# Revit family: Furniture-Lighted_Medicine_Cabinet-KOHLER-Family_Care-K-25237T_1
name_source: partatom
category: Lighting Fixtures
units: mm (PartAtom-declared; Revit-internal decimal feet)

## family parameters
Cut with Voids When Loaded = No
Host = Face
Light Source = Yes
Maintain Annotation Orientation = No
OmniClass Number = 23.25.53.11.13.11
OmniClass Title = Medicine Cabinet
Part Type = Normal
Room Calculation Point = No
Round Connector Dimension = Use Diameter
Shared = No

## types (2) — shared parameters
ADA Compliant = No
Apparent Load = 15 VA
Assembly Code = E2010
Color Filter = 16777215
Date Modified = 07/05/2022
Default Elevation = 60"
Dimming Lamp Color Temperature Shift = Incandescent Lamp Curve
Electrical Connector = Yes
Electrical Note = One Dedicated Circuit Required
Emit from Line Length = 24"
Finish = KOHLER-Metal-NA-Mild_Silver
Hardware Included = No
Height = 40 5/16"
Lamp = LED
Length = 6 1/16"
Light Source Symbol Size = 3"
Manufacturer = Kohler Co.
Master Format 2014 = 41 53 13
Master Format 2014 Name = Storage Cabinets
Material = Aluminium Construction
Product Documentation Link = https://files.kohler.com.cn
Product Name = Family Care
Product Page URL = https://www.kohler.com.cn
URL = http://www.kohler.com.cn
Voltage = 12 V
WaterSense Certified = No
Wattage Comments = 15W
Width = 22 13/16"

## per-type parameters (varying)
| type | Description | Left Door | Model | Right Door | Secondary Finish | Type |
| Left Door, NA-Mild Silver | Mirror Cabinet 600 mm (Left Door, Silver) | Yes | K-25237T-L-NA | No | Kohler-Plastic-7-Black_Black | 1 |
| Right Door, NA-Mild Silver | Mirror Cabinet 600 mm (Right Door, Silver) | No | K-25237T-R-NA | Yes | Kohler-Plastic-0-White | 2 |

## geometry (parser evidence)
native form markers: Sweep x4
no freeform markers — native parametric forms only
